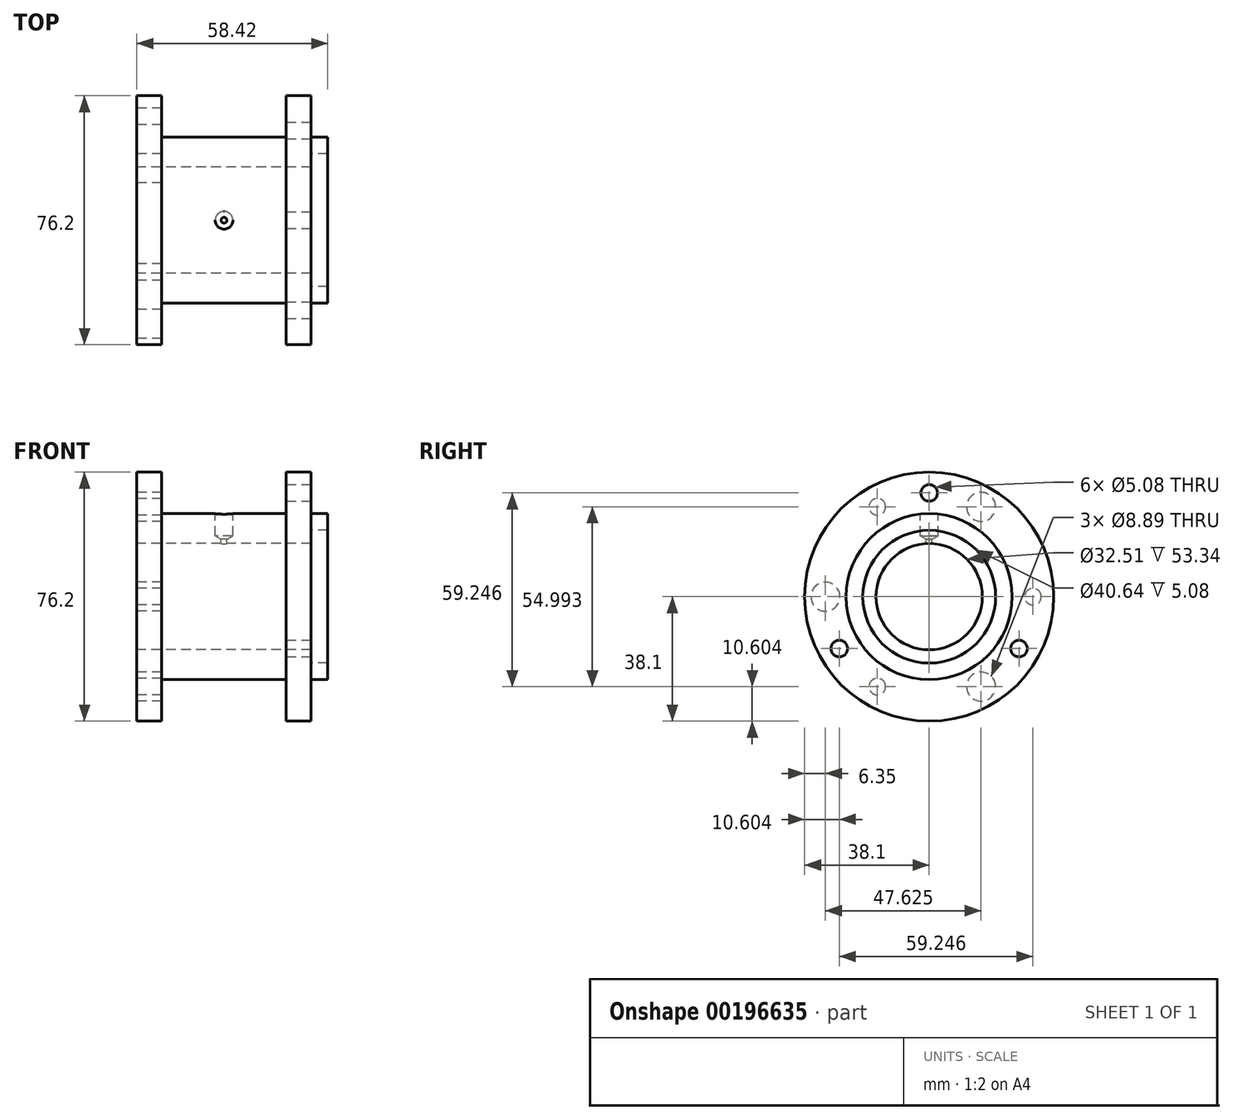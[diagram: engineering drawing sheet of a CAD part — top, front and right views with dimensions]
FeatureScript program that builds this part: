
annotation { "Feature Type Name" : "Feature", "Feature Type Description" : "" }
export const myFeature = defineFeature(function(context is Context, id is Id, definition is map)
    precondition{}
    {
        {
            var Q0;
            Q0=qCreatedBy(makeId("Front.planeOp"),FACE);
            var sketch = newSketch(context, id + "F0", { "sketchPlane" : qUnion([Q0])});
            skLineSegment(sketch, "E0.bottom", {"start": v(-19.05, -25.4) * mm, "end": v(19.05, -25.4) * mm});
            skLineSegment(sketch, "E0.top", {"start": v(-19.05, -16.26) * mm, "end": v(19.05, -16.26) * mm});
            skLineSegment(sketch, "E0.left", {"start": v(-19.05, -25.4) * mm, "end": v(-19.05, -16.26) * mm});
            skLineSegment(sketch, "E0.right", {"start": v(19.05, -25.4) * mm, "end": v(19.05, -16.26) * mm});
            skPoint(sketch, "E0.middle", {"position": v(0, -20.83) * mm});
            skSolve(sketch);
        }
        {
            var Q0;
            Q0=qCreatedBy(makeId("Front.planeOp"),FACE);
            var sketch = newSketch(context, id + "F1", { "sketchPlane" : qUnion([Q0])});
            skLineSegment(sketch, "E1", {"start": v(-54.66, 0) * mm, "end": v(61.53, 0) * mm});
            skSolve(sketch);
        }
        {
            var Q0;
            Q0=qSketchRegion(id+"F0",true);
            var Q1;
            Q1=sQuery(id+"F1.wireOp",EDGE,"E1");
            revolve(context, id + "F2", {"entities" : qUnion([Q0]), "axis" : qUnion([Q1]), "revolveType" : RevolveType.FULL});
        }
        {
            var Q0;
            Q0=qCreatedBy(makeId("Front.planeOp"),FACE);
            var sketch = newSketch(context, id + "F3", { "sketchPlane" : qUnion([Q0])});
            skLineSegment(sketch, "E2.bottom", {"start": v(-26.67, -38.1) * mm, "end": v(-19.05, -38.1) * mm});
            skLineSegment(sketch, "E2.top", {"start": v(-26.67, -16.26) * mm, "end": v(-19.05, -16.26) * mm});
            skLineSegment(sketch, "E2.left", {"start": v(-26.67, -38.1) * mm, "end": v(-26.67, -16.26) * mm});
            skLineSegment(sketch, "E2.right", {"start": v(-19.05, -38.1) * mm, "end": v(-19.05, -16.26) * mm});
            skPoint(sketch, "E2.middle", {"position": v(-22.86, -27.18) * mm});
            skSolve(sketch);
        }
        {
            var Q0;
            Q0 = qSketchRegion(id + "F3", true);
            var Q1;
            Q1=sQuery(id+"F1.wireOp",EDGE,"E1");
            revolve(context, id + "F4", {"operationType" : NewBodyOperationType.ADD, "entities" : qUnion([Q0]), "axis" : qUnion([Q1]), "revolveType" : RevolveType.FULL});
        }
        {
            var Q0;
            Q0=makeQuery(id+"F4.opRevolve","SWEPT_FACE",FACE,{"disambiguationData":[OSD([sQuery(id+"F3.wireOp",EDGE,"E2.left")])]});
            var sketch = newSketch(context, id + "F5", { "sketchPlane" : qUnion([Q0])});
            skCircle(sketch, "E3", {"center": v(31.75, 0) * mm, "radius": 4.45 * mm});
            skCircle(sketch, "E4", {"center": v(15.88, 27.5) * mm, "radius": 2.54 * mm});
            skCircle(sketch, "E5", {"center": v(-15.88, 27.5) * mm, "radius": 4.45 * mm});
            skCircle(sketch, "E6", {"center": v(-31.75, 0) * mm, "radius": 2.54 * mm});
            skCircle(sketch, "E7", {"center": v(-15.88, -27.5) * mm, "radius": 4.45 * mm});
            skCircle(sketch, "E8", {"center": v(15.88, -27.5) * mm, "radius": 2.54 * mm});
            skSolve(sketch);
        }
        {
            var Q0;
            Q0=qSketchRegion(id+"F5",true);
            var Q1;
            Q1=sQuery(id+"F5.wireOp",EDGE,"E3");
            var Q2;
            Q2=makeQuery(id+"F4.opRevolve","SWEPT_FACE",FACE,{"disambiguationData":[OSD([sQuery(id+"F3.wireOp",EDGE,"E2.right")])]});
            extrude(context, id + "F6", {"entities" : qUnion([Q0]), "operationType" : NewBodyOperationType.REMOVE, "surfaceEntities" : qUnion([Q1]), "oppositeDirection" : true, "endBoundEntityFace" : qUnion([Q2]), "depth" : 7.62 * mm});
        }
        {
            var Q0;
            Q0=qCreatedBy(makeId("Front.planeOp"),FACE);
            var sketch = newSketch(context, id + "F7", { "sketchPlane" : qUnion([Q0])});
            skLineSegment(sketch, "E9.bottom", {"start": v(19.05, -16.26) * mm, "end": v(26.67, -16.26) * mm});
            skLineSegment(sketch, "E9.top", {"start": v(19.05, -38.1) * mm, "end": v(26.67, -38.1) * mm});
            skLineSegment(sketch, "E9.left", {"start": v(19.05, -16.26) * mm, "end": v(19.05, -38.1) * mm});
            skLineSegment(sketch, "E9.right", {"start": v(26.67, -16.26) * mm, "end": v(26.67, -38.1) * mm});
            skSolve(sketch);
        }
        {
            var Q0;
            Q0=makeQuery(id+"F7.imprint","IMPRINT",FACE,{"disambiguationData":[TD([[makeQuery(id+"F7.imprint","IMPRINT",EDGE,{"derivedFrom":sQuery(id+"F7.wireOp",EDGE,"E9.bottom")}),-1.0]])]});
            var Q1;
            Q1=sQuery(id+"F1.wireOp",EDGE,"E1");
            revolve(context, id + "F8", {"operationType" : NewBodyOperationType.ADD, "entities" : qUnion([Q0]), "axis" : qUnion([Q1]), "revolveType" : RevolveType.FULL});
        }
        {
            var Q0;
            Q0=makeQuery(id+"F8.opRevolve","SWEPT_FACE",FACE,{"disambiguationData":[OSD([sQuery(id+"F7.wireOp",EDGE,"E9.right")])]});
            var sketch = newSketch(context, id + "F9", { "sketchPlane" : qUnion([Q0])});
            skCircle(sketch, "E10", {"center": v(0, 31.75) * mm, "radius": 2.54 * mm});
            skCircle(sketch, "E11", {"center": v(-27.5, -15.88) * mm, "radius": 2.54 * mm});
            skCircle(sketch, "E12", {"center": v(27.5, -15.88) * mm, "radius": 2.54 * mm});
            skSolve(sketch);
        }
        {
            var Q0;
            Q0 = qSketchRegion(id + "F9", true);
            extrude(context, id + "F10", {"entities" : qUnion([Q0]), "operationType" : NewBodyOperationType.REMOVE, "oppositeDirection" : true, "depth" : 7.62 * mm});
        }
        {
            var Q0;
            Q0=qCreatedBy(makeId("Front.planeOp"),FACE);
            var sketch = newSketch(context, id + "F11", { "sketchPlane" : qUnion([Q0])});
            skLineSegment(sketch, "E13.bottom", {"start": v(26.67, -20.32) * mm, "end": v(31.75, -20.32) * mm});
            skLineSegment(sketch, "E13.top", {"start": v(26.67, -25.4) * mm, "end": v(31.75, -25.4) * mm});
            skLineSegment(sketch, "E13.left", {"start": v(26.67, -20.32) * mm, "end": v(26.67, -25.4) * mm});
            skLineSegment(sketch, "E13.right", {"start": v(31.75, -20.32) * mm, "end": v(31.75, -25.4) * mm});
            skSolve(sketch);
        }
        {
            var Q0;
            Q0=makeQuery(id+"F11.imprint","IMPRINT",FACE,{"disambiguationData":[TD([[makeQuery(id+"F11.imprint","IMPRINT",EDGE,{"derivedFrom":sQuery(id+"F11.wireOp",EDGE,"E13.bottom")}),-1.0]])]});
            var Q1;
            Q1=sQuery(id+"F1.wireOp",EDGE,"E1");
            revolve(context, id + "F12", {"operationType" : NewBodyOperationType.ADD, "entities" : qUnion([Q0]), "axis" : qUnion([Q1]), "revolveType" : RevolveType.FULL});
        }
        {
            var Q0;
            Q0=qCreatedBy(makeId("Top.planeOp"),FACE);
            cPlane(context, id + "F13", {"entities" : qUnion([Q0]), "cplaneType" : CPlaneType.OFFSET, "offset" : 25.4 * mm, "width" : 152.4 * mm, "height" : 152.4 * mm});
        }
        {
            var Q0;
            Q0=qCreatedBy(id+"F13.planeOp",FACE);
            var sketch = newSketch(context, id + "F14", { "sketchPlane" : qUnion([Q0])});
            skPoint(sketch, "E14", {"position": v(0, 0) * mm});
            skSolve(sketch);
        }
        {
            var Q0;
            Q0=sQuery(id+"F14.wireOp",VERTEX,"E14");
            var Q1;
            Q1=makeQuery(id+"F2.opRevolve","SWEPT_BODY",BODY,{"disambiguationData":[OSD([sQuery(id+"F0.wireOp",EDGE,"E0.bottom"),sQuery(id+"F0.wireOp",EDGE,"E0.top"),sQuery(id+"F0.wireOp",EDGE,"E0.left"),sQuery(id+"F0.wireOp",EDGE,"E0.right")])]});
            hole(context, id + "F15", {"style" : HoleStyle.SIMPLE, "endStyle" : HoleEndStyle.BLIND, "standardTappedOrClearance" : lookupTablePath({ "standard" : "ANSI", "engagement" : "75%", "pitch" : "28 tpi", "size" : "1/4", "type" : "Tapped" }), "standardBlindInLast" : lookupTablePath({ "standard" : "ANSI", "engagement" : "75%", "pitch" : "28 tpi", "size" : "1/4", "type" : "Tapped" }), "holeDiameter" : 5.4 * mm, "holeDepth" : 6.6 * mm, "locations" : qUnion([Q0]), "scope" : qUnion([Q1]), "majorDiameter" : 6.35 * mm});
        }
        {
            var Q0;
            Q0=sQuery(id+"F14.wireOp",VERTEX,"E14");
            var Q1;
            Q1=makeQuery(id+"F2.opRevolve","SWEPT_BODY",BODY,{"disambiguationData":[OSD([sQuery(id+"F0.wireOp",EDGE,"E0.bottom"),sQuery(id+"F0.wireOp",EDGE,"E0.top"),sQuery(id+"F0.wireOp",EDGE,"E0.left"),sQuery(id+"F0.wireOp",EDGE,"E0.right")])]});
            hole(context, id + "F16", {"style" : HoleStyle.SIMPLE, "endStyle" : HoleEndStyle.BLIND, "holeDiameter" : 1.78 * mm, "holeDepth" : 9.14 * mm, "locations" : qUnion([Q0]), "scope" : qUnion([Q1])});
        }
    });
